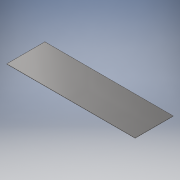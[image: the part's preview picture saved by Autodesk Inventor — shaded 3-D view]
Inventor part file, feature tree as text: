
AUTODESK INVENTOR PART (.ipt)
format: ipt  version: 2017 (Build 210142000, 142)  size: 101,376 bytes
history: native  units: mm
features: reference x3, other x3, plane x1, sheet_metal_op x1, sketch x1
ambient origin geometry x8: Origin, YZ Plane, XZ Plane, XY Plane, X Axis, Y Axis, Z Axis, Center Point
bodies: Solid1 (feature_tree)
feature tree (9):
  plane  "Work Plane1"
  sheet_metal_op  "Face1"
  sketch  "Sketch1"  dims[d0=1.5mm]
  reference  "Reference1"
  reference  "Reference2"
  reference  "Reference3"
  other  "Plate1"
  other  "Bancada de Lavagem Mãos - 1150 x 370 x 900h.iam"
  other  "Bancada Lavagem de Mãos:1"
